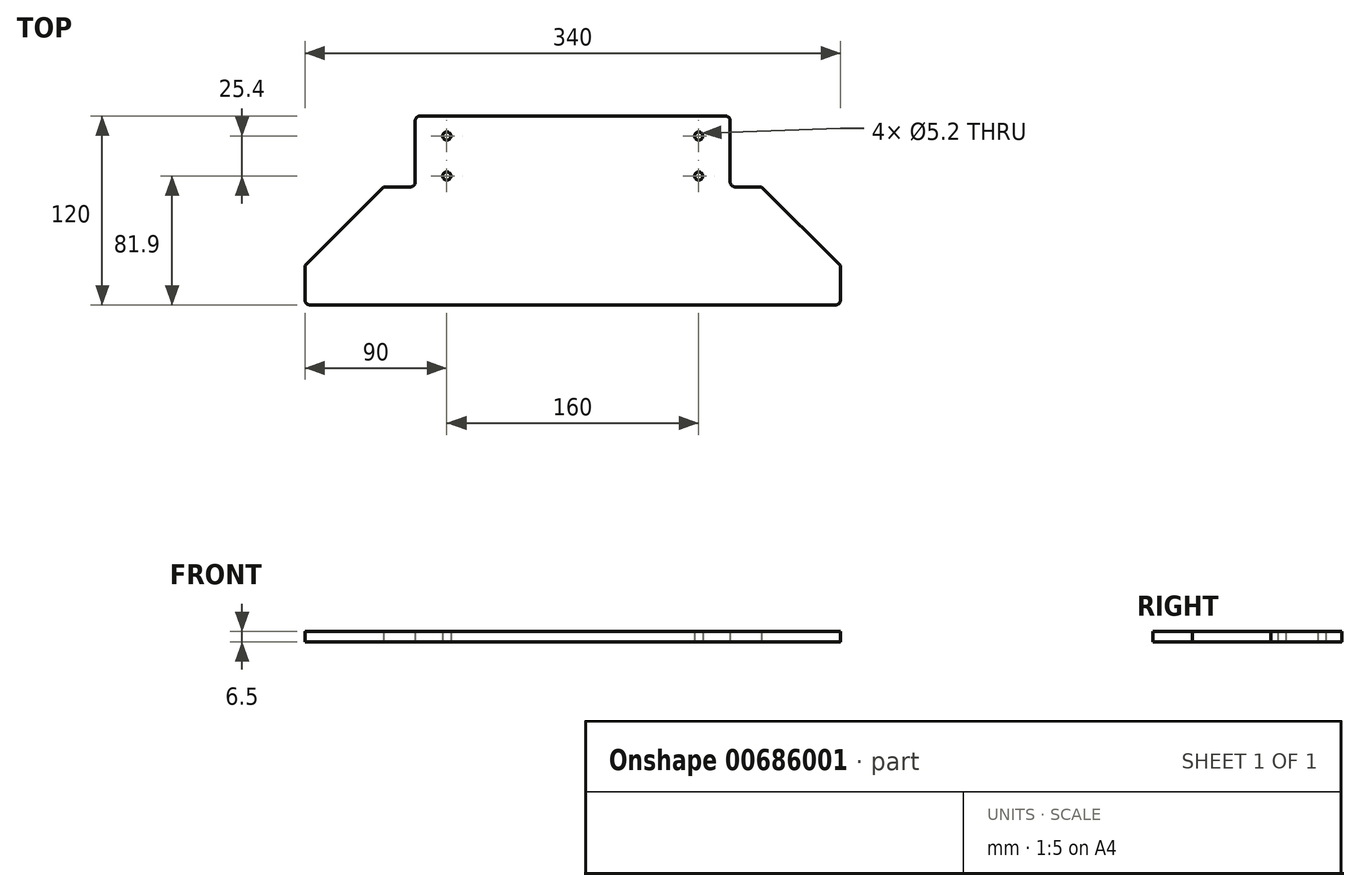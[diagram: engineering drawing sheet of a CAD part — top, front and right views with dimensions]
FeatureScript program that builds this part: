
annotation { "Feature Type Name" : "Feature", "Feature Type Description" : "" }
export const myFeature = defineFeature(function(context is Context, id is Id, definition is map)
    precondition{}
    {
        {
            var Q0;
            Q0=qCreatedBy(makeId("Top.planeOp"),FACE);
            var sketch = newSketch(context, id + "F0", { "sketchPlane" : qUnion([Q0])});
            skLineSegment(sketch, "E0", {"start": v(-120, 75) * mm, "end": v(-170, 25) * mm});
            skLineSegment(sketch, "E1", {"start": v(-170, 25) * mm, "end": v(-170, 3) * mm});
            skLineSegment(sketch, "E2", {"start": v(-167, 0) * mm, "end": v(0, 0) * mm});
            skLineSegment(sketch, "E3", {"start": v(-112.56, 107.3) * mm, "end": v(0, 107.3) * mm, "construction": true});
            skCircle(sketch, "E4", {"center": v(-80, 107.3) * mm, "radius": 2.6 * mm});
            skLineSegment(sketch, "E5.MirrorCS", {"start": v(167, 0) * mm, "end": v(0, 0) * mm});
            skLineSegment(sketch, "E6.MirrorCS", {"start": v(170, 25) * mm, "end": v(170, 3) * mm});
            skLineSegment(sketch, "E7.MirrorCS", {"start": v(120, 75) * mm, "end": v(170, 25) * mm});
            skCircle(sketch, "E8.MirrorC", {"center": v(80, 107.3) * mm, "radius": 2.6 * mm});
            skLineSegment(sketch, "E9", {"start": v(-120, 75) * mm, "end": v(-103, 75) * mm});
            skLineSegment(sketch, "E10", {"start": v(-100, 78) * mm, "end": v(-100, 117) * mm});
            skLineSegment(sketch, "E11", {"start": v(0, 120) * mm, "end": v(-97, 120) * mm});
            skLineSegment(sketch, "E12.MirrorCS", {"start": v(100, 78) * mm, "end": v(100, 117) * mm});
            skLineSegment(sketch, "E13.MirrorCS", {"start": v(0, 120) * mm, "end": v(97, 120) * mm});
            skLineSegment(sketch, "E14.MirrorCS", {"start": v(120, 75) * mm, "end": v(103, 75) * mm});
            skLineSegment(sketch, "E15", {"start": v(0, 81.9) * mm, "end": v(-108.75, 81.9) * mm, "construction": true});
            skCircle(sketch, "E16", {"center": v(-80, 81.9) * mm, "radius": 2.6 * mm});
            skCircle(sketch, "E17.MirrorC", {"center": v(80, 81.9) * mm, "radius": 2.6 * mm});
            skPoint(sketch, "E18.visualSharp", {"position": v(100, 120) * mm});
            skArc(sketch, "E18.filletArc", {"start": v(100, 117) * mm, "mid": v(99.12, 119.12) * mm, "end": v(97, 120) * mm});
            skPoint(sketch, "E19.visualSharp", {"position": v(-100, 120) * mm});
            skArc(sketch, "E19.filletArc", {"start": v(-97, 120) * mm, "mid": v(-99.12, 119.12) * mm, "end": v(-100, 117) * mm});
            skPoint(sketch, "E20.visualSharp", {"position": v(170, 0) * mm});
            skArc(sketch, "E20.filletArc", {"start": v(167, 0) * mm, "mid": v(169.12, 0.88) * mm, "end": v(170, 3) * mm});
            skPoint(sketch, "E21.visualSharp", {"position": v(-170, 0) * mm});
            skArc(sketch, "E21.filletArc", {"start": v(-170, 3) * mm, "mid": v(-169.12, 0.88) * mm, "end": v(-167, 0) * mm});
            skPoint(sketch, "E22.visualSharp", {"position": v(-100, 75) * mm});
            skArc(sketch, "E22.filletArc", {"start": v(-103, 75) * mm, "mid": v(-100.88, 75.88) * mm, "end": v(-100, 78) * mm});
            skPoint(sketch, "E23.visualSharp", {"position": v(100, 75) * mm});
            skArc(sketch, "E23.filletArc", {"start": v(100, 78) * mm, "mid": v(100.88, 75.88) * mm, "end": v(103, 75) * mm});
            skSolve(sketch);
        }
        {
            var Q0;
            Q0 = qSketchRegion(id + "F0", true);
            extrude(context, id + "F1", {"entities" : qUnion([Q0]), "depth" : 6.5 * mm, "offsetDistance" : 25 * mm});
        }
    });
